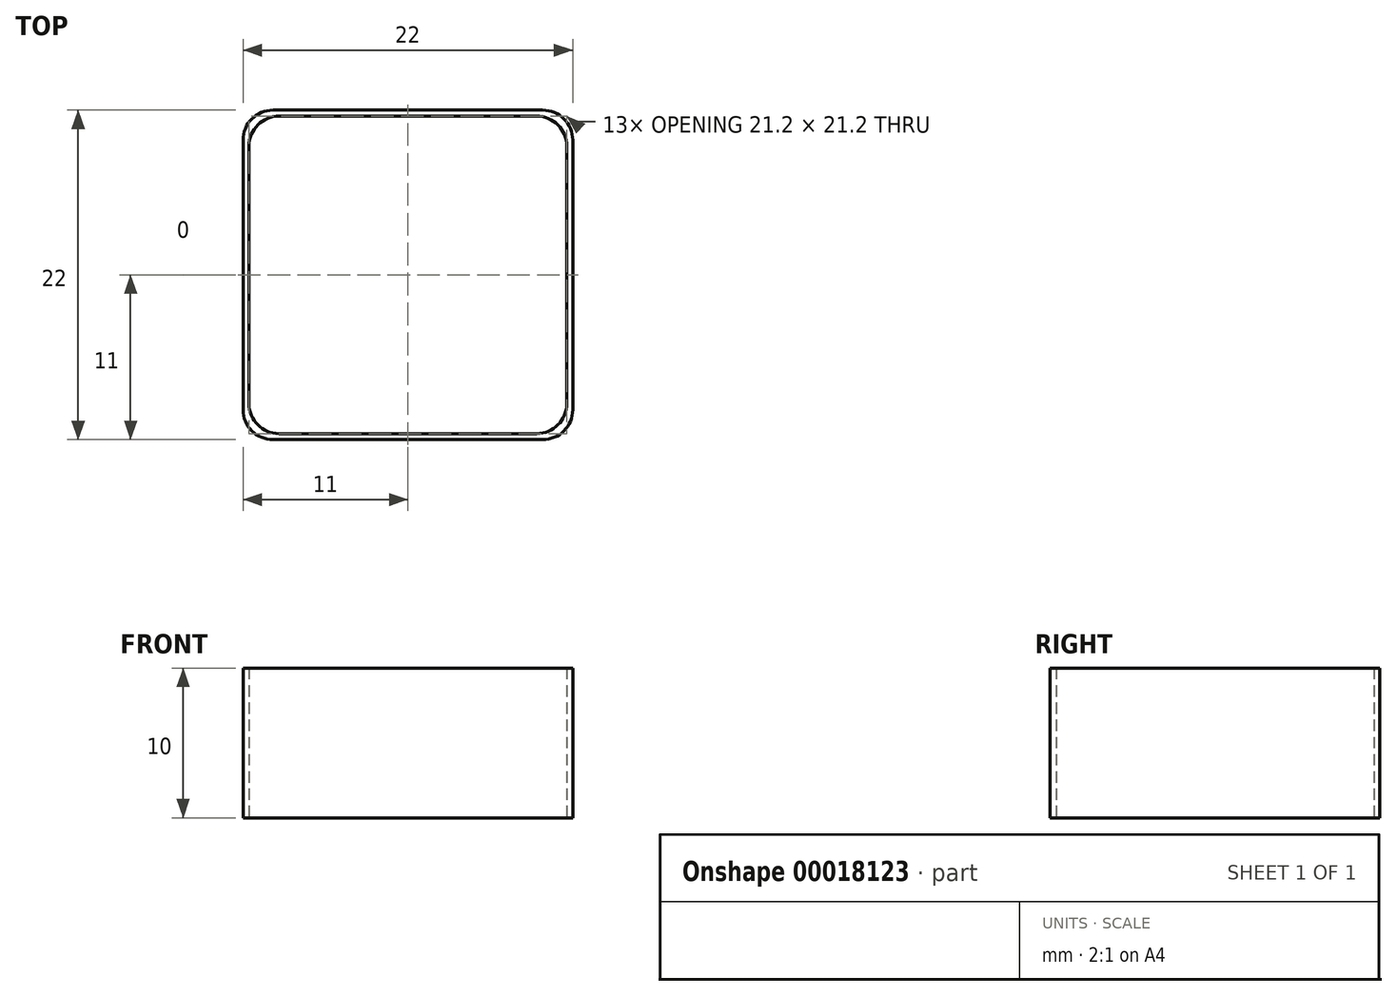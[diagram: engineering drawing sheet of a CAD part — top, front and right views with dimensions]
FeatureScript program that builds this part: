
annotation { "Feature Type Name" : "Feature", "Feature Type Description" : "" }
export const myFeature = defineFeature(function(context is Context, id is Id, definition is map)
    precondition{}
    {
        {
            var Q0;
            Q0=qCreatedBy(makeId("Top.planeOp"),FACE);
            var sketch = newSketch(context, id + "F0", { "sketchPlane" : qUnion([Q0])});
            skLineSegment(sketch, "E0.bottom", {"start": v(0, 0) * mm, "end": v(22, 0) * mm});
            skLineSegment(sketch, "E0.top", {"start": v(0, 22) * mm, "end": v(22, 22) * mm});
            skLineSegment(sketch, "E0.left", {"start": v(0, 0) * mm, "end": v(0, 22) * mm});
            skLineSegment(sketch, "E0.right", {"start": v(22, 0) * mm, "end": v(22, 22) * mm});
            skLineSegment(sketch, "E1", {"start": v(0, 11) * mm, "end": v(22, 11) * mm, "construction": true});
            skLineSegment(sketch, "E2", {"start": v(11, 22) * mm, "end": v(11, 0) * mm, "construction": true});
            skLineSegment(sketch, "E3.bottom", {"start": v(0.4, 21.6) * mm, "end": v(21.6, 21.6) * mm});
            skLineSegment(sketch, "E3.top", {"start": v(0.4, 0.4) * mm, "end": v(21.6, 0.4) * mm});
            skLineSegment(sketch, "E3.left", {"start": v(0.4, 21.6) * mm, "end": v(0.4, 0.4) * mm});
            skLineSegment(sketch, "E3.right", {"start": v(21.6, 21.6) * mm, "end": v(21.6, 0.4) * mm});
            skSolve(sketch);
        }
        {
            var Q0;
            Q0=makeQuery(id+"F0.imprint","IMPRINT",FACE,{"disambiguationData":[TD([[makeQuery(id+"F0.imprint","IMPRINT",EDGE,{"derivedFrom":sQuery(id+"F0.wireOp",EDGE,"E0.bottom")}),1.0]])]});
            extrude(context, id + "F1", {"entities" : qUnion([Q0]), "depth" : 10 * mm});
        }
        {
            var Q0;
            Q0=makeQuery(id+"F1.opExtrude","SWEPT_EDGE",EDGE,{"disambiguationData":[OSD([sQuery(id+"F0.wireOp",EDGE,"E0.bottom"),sQuery(id+"F0.wireOp",EDGE,"E0.right")])]});
            var Q1;
            Q1=makeQuery(id+"F1.opExtrude","SWEPT_EDGE",EDGE,{"disambiguationData":[OSD([sQuery(id+"F0.wireOp",EDGE,"E0.top"),sQuery(id+"F0.wireOp",EDGE,"E0.right")])]});
            var Q2;
            Q2=makeQuery(id+"F1.opExtrude","SWEPT_EDGE",EDGE,{"disambiguationData":[OSD([sQuery(id+"F0.wireOp",EDGE,"E0.top"),sQuery(id+"F0.wireOp",EDGE,"E0.left")])]});
            var Q3;
            Q3=makeQuery(id+"F1.opExtrude","SWEPT_EDGE",EDGE,{"disambiguationData":[OSD([sQuery(id+"F0.wireOp",EDGE,"E0.bottom"),sQuery(id+"F0.wireOp",EDGE,"E0.left")])]});
            var Q4;
            Q4=makeQuery(id+"F1.opExtrude","SWEPT_EDGE",EDGE,{"disambiguationData":[OSD([sQuery(id+"F0.wireOp",EDGE,"E3.top"),sQuery(id+"F0.wireOp",EDGE,"E3.left")])]});
            var Q5;
            Q5=makeQuery(id+"F1.opExtrude","SWEPT_EDGE",EDGE,{"disambiguationData":[OSD([sQuery(id+"F0.wireOp",EDGE,"E3.bottom"),sQuery(id+"F0.wireOp",EDGE,"E3.left")])]});
            var Q6;
            Q6=makeQuery(id+"F1.opExtrude","SWEPT_EDGE",EDGE,{"disambiguationData":[OSD([sQuery(id+"F0.wireOp",EDGE,"E3.top"),sQuery(id+"F0.wireOp",EDGE,"E3.right")])]});
            var Q7;
            Q7=makeQuery(id+"F1.opExtrude","SWEPT_EDGE",EDGE,{"disambiguationData":[OSD([sQuery(id+"F0.wireOp",EDGE,"E3.bottom"),sQuery(id+"F0.wireOp",EDGE,"E3.right")])]});
            fillet(context, id + "F2", {"entities" : qUnion([Q0, Q1, Q2, Q3, Q4, Q5, Q6, Q7]), "radius" : 2 * mm, "tangentPropagation" : true, "allowEdgeOverflow" : false});
        }
    });
